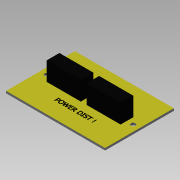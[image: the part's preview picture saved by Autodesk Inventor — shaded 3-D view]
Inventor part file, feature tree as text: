
AUTODESK INVENTOR PART (.ipt)
format: ipt  version: 2015 SP1 (Build 190203100, 203)  size: 108,544 bytes
history: native  units: mm
features: sketch x2, extrude x2
ambient origin geometry x8: Origin, YZ Plane, XZ Plane, XY Plane, X Axis, Y Axis, Z Axis, Center Point
bodies: Solid1 (feature_tree)
feature tree (4):
  sketch  "Sketch1"  dims[d0=78.56mm d1=54.61mm]
  extrude  "Extrusion1"  Depth=54.61mm
  extrude  "Extrusion2"  Depth=68.56mm
  sketch  "Sketch2"  dims[d2=3.5mm d3=5.0mm d4=3.5mm d5=5.0mm d6=27.0mm d7=10.0mm d8=5.0mm d9=27.0mm d10=10.0mm d11=5.0mm d12=1.7mm d13=0.0mm d14=16.58mm d15=0.0mm d16=68.56mm]
